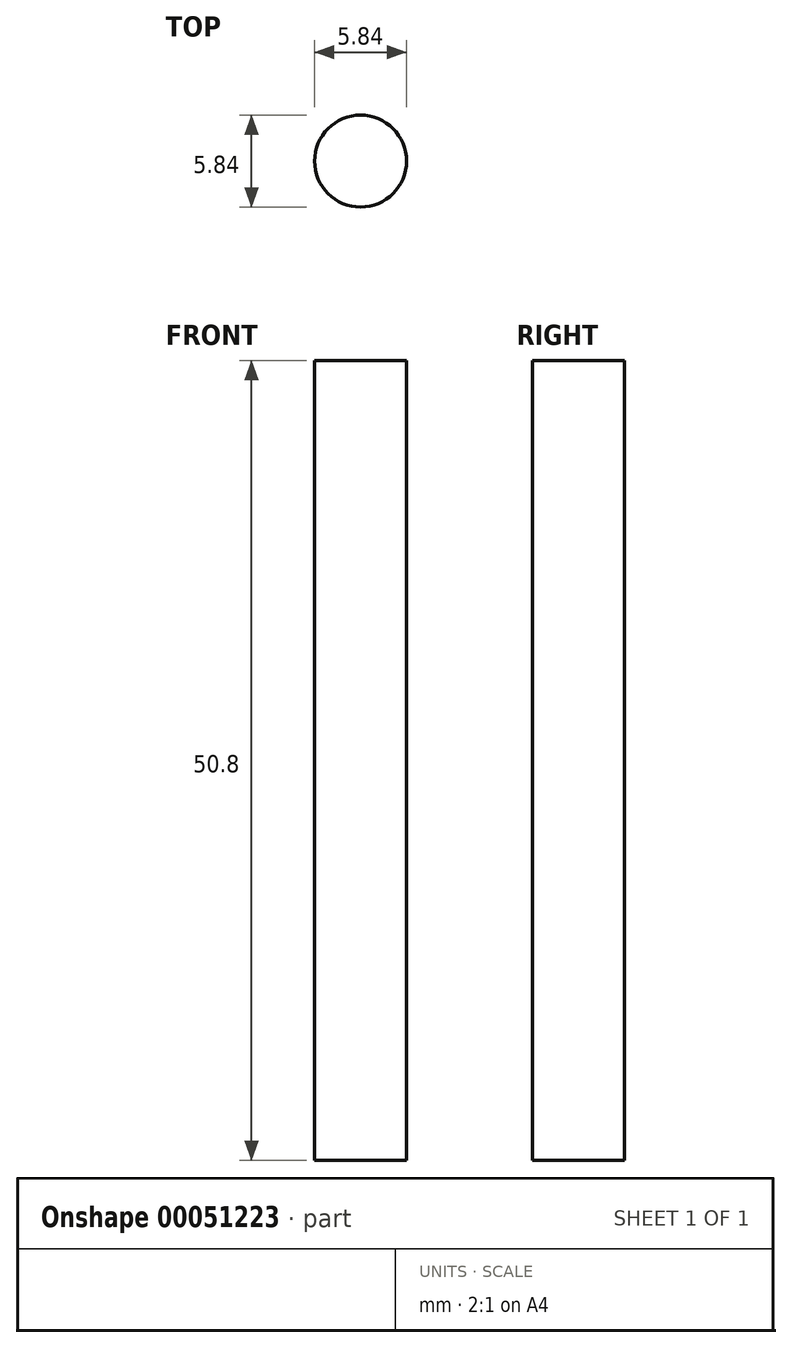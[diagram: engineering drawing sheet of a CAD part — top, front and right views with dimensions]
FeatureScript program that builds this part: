
annotation { "Feature Type Name" : "Feature", "Feature Type Description" : "" }
export const myFeature = defineFeature(function(context is Context, id is Id, definition is map)
    precondition{}
    {
        {
            var Q0;
            Q0=qCreatedBy(makeId("Top.planeOp"),FACE);
            var sketch = newSketch(context, id + "F0", { "sketchPlane" : qUnion([Q0])});
            skCircle(sketch, "E0", {"center": v(0, 0) * mm, "radius": 2.92 * mm});
            skSolve(sketch);
        }
        {
            var Q0;
            Q0 = qSketchRegion(id + "F0", true);
            extrude(context, id + "F1", {"entities" : qUnion([Q0]), "depth" : 50.8 * mm});
        }
    });
